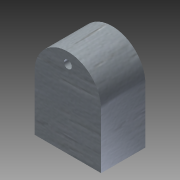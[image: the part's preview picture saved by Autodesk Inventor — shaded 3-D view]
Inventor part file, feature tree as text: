
AUTODESK INVENTOR PART (.ipt)
format: ipt  version: 2011 SP1 (Build 150282100, 282)  size: 97,280 bytes
history: native  units: in
note: dims shown in document units (in); Inventor stores cm internally (conversion verified against a paired STEP export)
features: extrude x1, hole x1, sketch x1
ambient origin geometry x8: Origin, YZ Plane, XZ Plane, XY Plane, X Axis, Y Axis, Z Axis, Center Point
bodies: Solid1 (feature_tree)
feature tree (3):
  extrude  "Extrusion1"  Depth=0.375in
  hole  "Hole1"  [1 undecoded]
  sketch  "Sketch1"  dims[d0=0.75in d1=0.375in d2=0.375in d3=0.625in d7=0.5in d8=0.0in d9=0.375in d10=0.875in d11=0.089in d12=0.75in d13=0.375in d14=0.25in d15=0.5635in d16=0.25in d17=0.0in]
note: 1 required parameter value undecoded (feature->parameter linkage not recoverable at this tier; creation-order binding heuristic only, values carry confidence <= 0.55)
